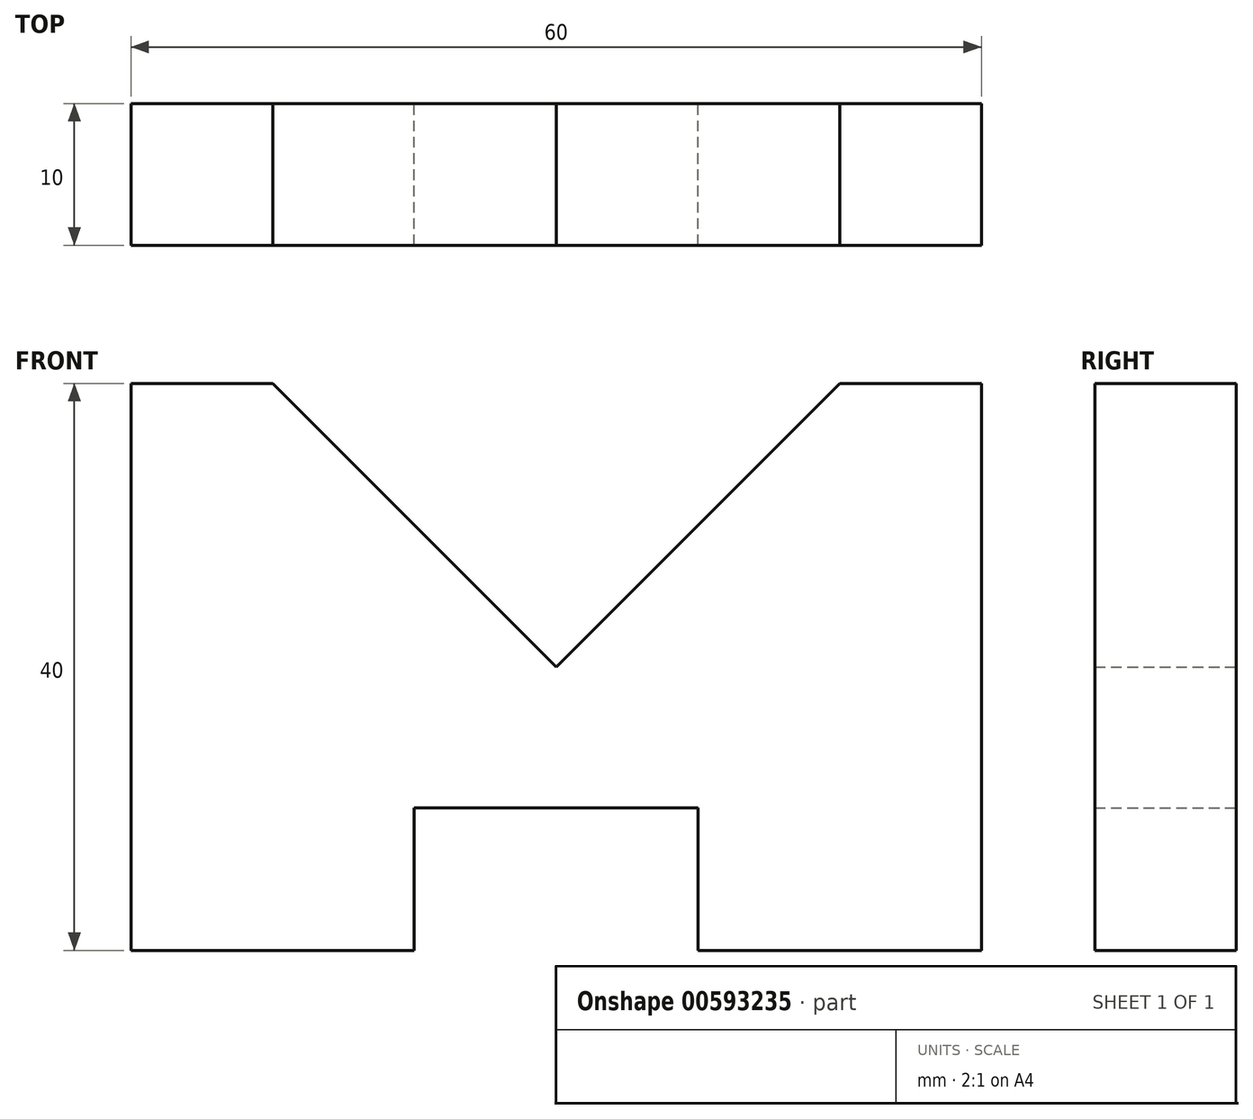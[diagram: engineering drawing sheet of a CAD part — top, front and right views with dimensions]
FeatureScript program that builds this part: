
annotation { "Feature Type Name" : "Feature", "Feature Type Description" : "" }
export const myFeature = defineFeature(function(context is Context, id is Id, definition is map)
    precondition{}
    {
        {
            var Q0;
            Q0=qCreatedBy(makeId("Front.planeOp"),FACE);
            var sketch = newSketch(context, id + "F0", { "sketchPlane" : qUnion([Q0])});
            skLineSegment(sketch, "E0", {"start": v(0, 0) * mm, "end": v(0, 40) * mm});
            skLineSegment(sketch, "E1", {"start": v(0, 40) * mm, "end": v(10, 40) * mm});
            skLineSegment(sketch, "E2", {"start": v(10, 40) * mm, "end": v(30, 20) * mm});
            skLineSegment(sketch, "E3", {"start": v(30, 20) * mm, "end": v(50, 40) * mm});
            skLineSegment(sketch, "E4", {"start": v(50, 40) * mm, "end": v(60, 40) * mm});
            skLineSegment(sketch, "E5", {"start": v(60, 40) * mm, "end": v(60, 0) * mm});
            skLineSegment(sketch, "E6", {"start": v(60, 0) * mm, "end": v(40.02, 0) * mm});
            skLineSegment(sketch, "E7", {"start": v(40.02, 0) * mm, "end": v(40.02, 10.04) * mm});
            skLineSegment(sketch, "E8", {"start": v(40.02, 10.04) * mm, "end": v(19.98, 10.04) * mm});
            skLineSegment(sketch, "E9", {"start": v(19.98, 10.04) * mm, "end": v(19.98, 0) * mm});
            skLineSegment(sketch, "E10", {"start": v(19.98, 0) * mm, "end": v(0, 0) * mm});
            skSolve(sketch);
        }
        {
            var Q0;
            Q0=makeQuery(id+"F0.imprint","IMPRINT",FACE,{"disambiguationData":[TD([[makeQuery(id+"F0.imprint","IMPRINT",EDGE,{"derivedFrom":sQuery(id+"F0.wireOp",EDGE,"E0")}),-1.0]])]});
            extrude(context, id + "F1", {"entities" : qUnion([Q0]), "depth" : 10 * mm, "offsetDistance" : 25.4 * mm});
        }
    });
